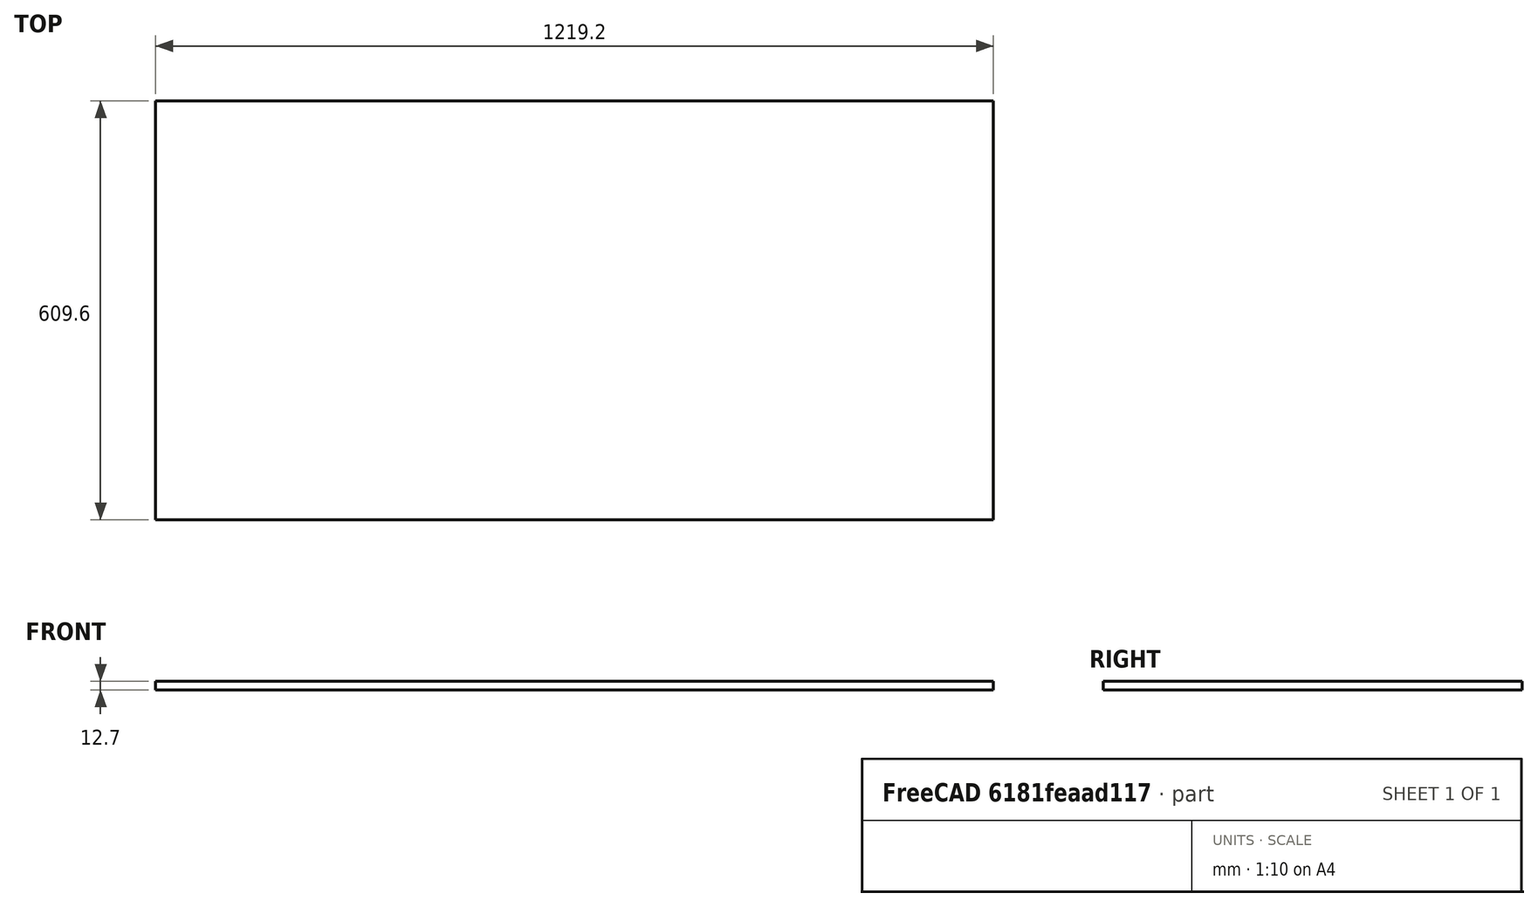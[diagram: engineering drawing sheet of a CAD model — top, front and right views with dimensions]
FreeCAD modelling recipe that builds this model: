
FCSTD DOCUMENT  (FreeCAD 0.17R11141 (Git))
Label: shelf_24x48in
License: All rights reserved
LicenseURL: http://en.wikipedia.org/wiki/All_rights_reserved
objects: Sketcher::SketchObject×1, PartDesign::Pad×1, PartDesign::Body×1
note: 4 computed .brp shape members not serialized (recipe doc carries the construction recipe); baked Part::Feature solids carry a one-line shape summary decoded from their .brp

FEATURE [Sketcher::SketchObject] Sketch
  MapMode = 5
  Support = -> [XY_Plane]
  sketch-geometry (4):
    g0: LineSegment StartX=0 StartY=0 StartZ=0 EndX=1219.2 EndY=0 EndZ=0
    g1: LineSegment StartX=1219.2 StartY=0 StartZ=0 EndX=1219.2 EndY=609.6 EndZ=0
    g2: LineSegment StartX=1219.2 StartY=609.6 StartZ=0 EndX=0 EndY=609.6 EndZ=0
    g3: LineSegment StartX=0 StartY=609.6 StartZ=0 EndX=0 EndY=0 EndZ=0
  constraints (11):
    c: Coincident(g0,g1)
    c: Coincident(g1,g2)
    c: Coincident(g2,g3)
    c: Coincident(g3,g0)
    c: Horizontal(g0)
    c: Horizontal(g2)
    c: Vertical(g1)
    c: Vertical(g3)
    c: Coincident(g0,g-1)
    c: DistanceY(g3,g3) = 609.6
    c: DistanceX(g0,g0) = 1219.2
FEATURE [PartDesign::Pad] Pad
  Length = 12.7
  Length2 = 100
  Profile = -> Sketch
  Type = 0
FEATURE [PartDesign::Body] Body
  Group = -> [Sketch,Pad]
  Origin = -> BodyOrigin
  Tip = -> Pad
